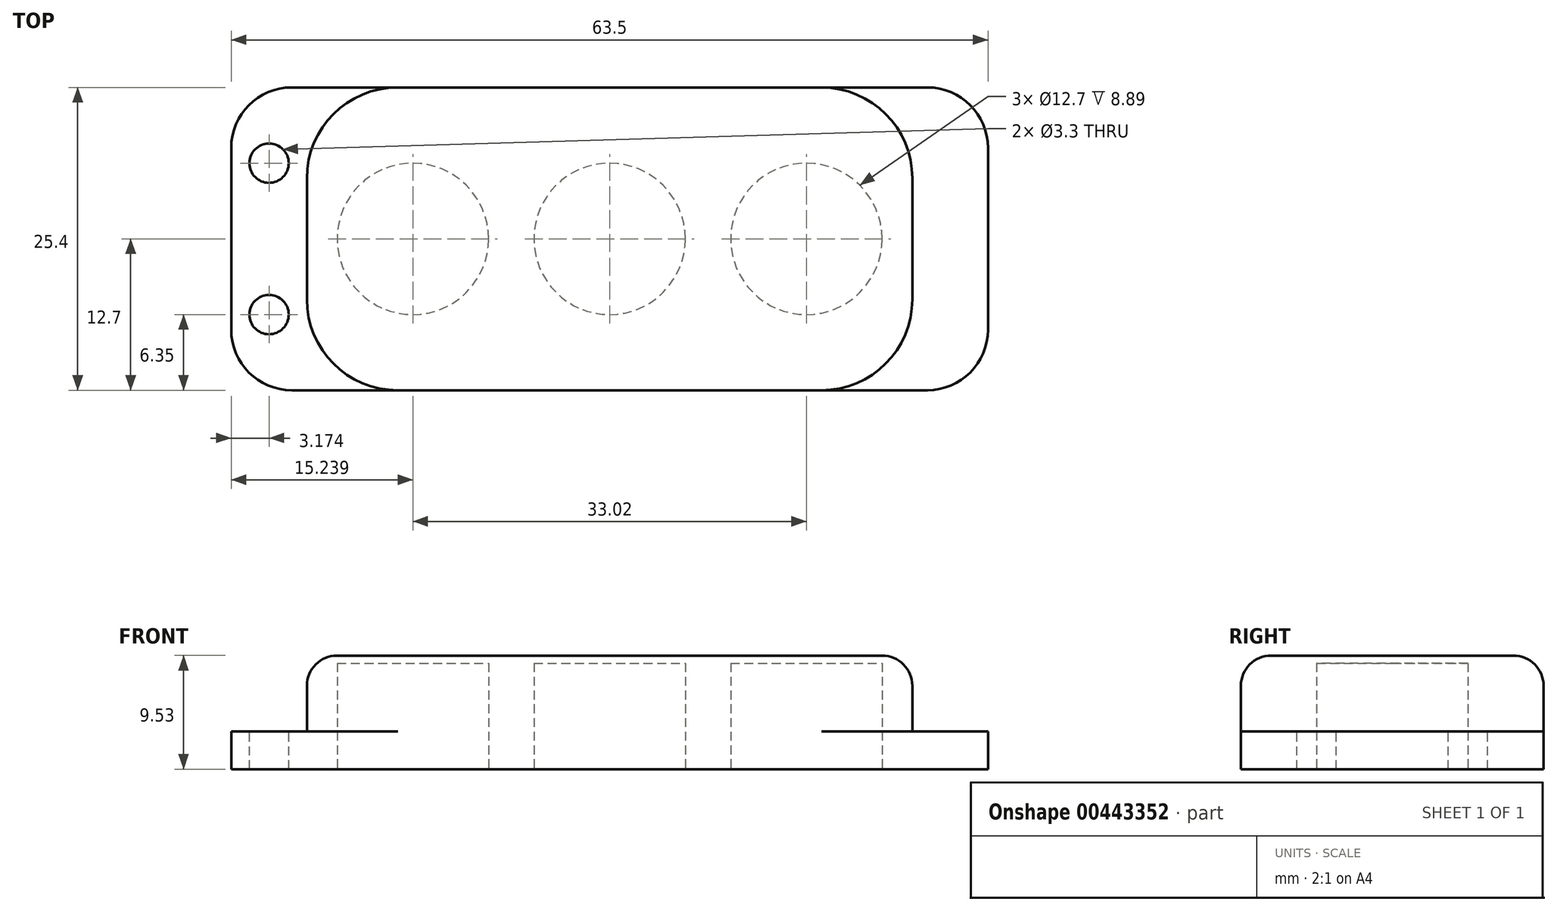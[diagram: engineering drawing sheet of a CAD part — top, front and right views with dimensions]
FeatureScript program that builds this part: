
annotation { "Feature Type Name" : "Feature", "Feature Type Description" : "" }
export const myFeature = defineFeature(function(context is Context, id is Id, definition is map)
    precondition{}
    {
        {
            var Q0;
            Q0=qCreatedBy(makeId("Front.planeOp"),FACE);
            var sketch = newSketch(context, id + "F0", { "sketchPlane" : qUnion([Q0])});
            skLineSegment(sketch, "E0.bottom", {"start": v(-44, 0) * mm, "end": v(19.5, 0) * mm});
            skLineSegment(sketch, "E0.top", {"start": v(-37.64, 9.52) * mm, "end": v(13.16, 9.52) * mm});
            skLineSegment(sketch, "E0.left", {"start": v(-44, 0) * mm, "end": v(-44, 3.18) * mm});
            skLineSegment(sketch, "E0.right", {"start": v(19.5, 0) * mm, "end": v(19.5, 3.17) * mm});
            skLineSegment(sketch, "E1.top", {"start": v(-44, 3.17) * mm, "end": v(-37.64, 3.17) * mm});
            skLineSegment(sketch, "E1.right", {"start": v(-37.64, 9.52) * mm, "end": v(-37.64, 3.17) * mm});
            skLineSegment(sketch, "E2.top", {"start": v(19.5, 3.17) * mm, "end": v(13.16, 3.17) * mm});
            skLineSegment(sketch, "E2.right", {"start": v(13.16, 9.52) * mm, "end": v(13.16, 3.17) * mm});
            skLineSegment(sketch, "E3", {"start": v(-12.24, 9.52) * mm, "end": v(-12.24, 0) * mm, "construction": true});
            skSolve(sketch);
        }
        {
            var Q0;
            Q0 = qSketchRegion(id + "F0", true);
            extrude(context, id + "F1", {"entities" : qUnion([Q0]), "depth" : 25.4 * mm});
        }
        {
            var Q0;
            Q0=makeQuery(id+"F1.opExtrude","SWEPT_FACE",FACE,{"disambiguationData":[OSD([sQuery(id+"F0.wireOp",EDGE,"E0.top")])]});
            var sketch = newSketch(context, id + "F2", { "sketchPlane" : qUnion([Q0])});
            skPoint(sketch, "E4", {"position": v(4.27, -12.7) * mm});
            skPoint(sketch, "E5", {"position": v(-28.75, -12.7) * mm});
            skCircle(sketch, "E6", {"center": v(-28.75, -12.7) * mm, "radius": 6.48 * mm});
            skCircle(sketch, "E7", {"center": v(4.27, -12.7) * mm, "radius": 6.48 * mm});
            skSolve(sketch);
        }
        {
            var Q0;
            Q0=makeQuery(id+"F1.opExtrude","SWEPT_FACE",FACE,{"disambiguationData":[OSD([sQuery(id+"F0.wireOp",EDGE,"E1.top")])]});
            var sketch = newSketch(context, id + "F3", { "sketchPlane" : qUnion([Q0])});
            skPoint(sketch, "E8", {"position": v(-40.82, -19.05) * mm});
            skPoint(sketch, "E9", {"position": v(-40.82, -6.35) * mm});
            skCircle(sketch, "E10", {"center": v(-40.82, -19.05) * mm, "radius": 1.65 * mm});
            skCircle(sketch, "E11", {"center": v(-40.82, -6.35) * mm, "radius": 1.65 * mm});
            skPoint(sketch, "E12.0", {"position": v(-12.24, -25.4) * mm});
            skLineSegment(sketch, "E13", {"start": v(-12.24, -25.4) * mm, "end": v(-12.24, 0) * mm});
            skCircle(sketch, "E14.MirrorC", {"center": v(16.33, -6.35) * mm, "radius": 1.65 * mm});
            skCircle(sketch, "E15.MirrorC", {"center": v(16.33, -19.05) * mm, "radius": 1.65 * mm});
            skSolve(sketch);
        }
        {
            var Q0;
            Q0=makeQuery(id+"F3.imprint","IMPRINT",FACE,{"disambiguationData":[TD([[makeQuery(id+"F3.imprint","IMPRINT",EDGE,{"derivedFrom":sQuery(id+"F3.wireOp",EDGE,"E10")}),1.0]])]});
            var Q1;
            Q1=makeQuery(id+"F3.imprint","IMPRINT",FACE,{"disambiguationData":[TD([[makeQuery(id+"F3.imprint","IMPRINT",EDGE,{"derivedFrom":sQuery(id+"F3.wireOp",EDGE,"E11")}),1.0]])]});
            var Q2;
            Q2=makeQuery(id+"F3.imprint","IMPRINT",FACE,{"disambiguationData":[TD([[makeQuery(id+"F3.imprint","IMPRINT",EDGE,{"derivedFrom":sQuery(id+"F3.wireOp",EDGE,"fb4f4f7a-e8af-40d2-be97-37f52cc8ef450.MirrorC")}),-1.0]])]});
            var Q3;
            Q3=makeQuery(id+"F3.imprint","IMPRINT",FACE,{"disambiguationData":[TD([[makeQuery(id+"F3.imprint","IMPRINT",EDGE,{"derivedFrom":sQuery(id+"F3.wireOp",EDGE,"d004ccc5-d1c6-44e7-8c95-f3ccb0f429bf0.MirrorC")}),-1.0]])]});
            var Q4;
            Q4=makeQuery(id+"F3.imprint","IMPRINT",FACE,{"disambiguationData":[TD([[makeQuery(id+"F3.imprint","IMPRINT",EDGE,{"derivedFrom":sQuery(id+"F3.wireOp",EDGE,"E14.MirrorC")}),-1.0]])]});
            var Q5;
            Q5=makeQuery(id+"F3.imprint","IMPRINT",FACE,{"disambiguationData":[TD([[makeQuery(id+"F3.imprint","IMPRINT",EDGE,{"derivedFrom":sQuery(id+"F3.wireOp",EDGE,"E15.MirrorC")}),-1.0]])]});
            extrude(context, id + "F4", {"entities" : qUnion([Q0, Q1, Q2, Q3, Q4, Q5]), "operationType" : NewBodyOperationType.REMOVE, "endBound" : BoundingType.THROUGH_ALL, "oppositeDirection" : true, "depth" : 25.4 * mm});
        }
        {
            var Q0;
            Q0=makeQuery(id+"F1.opExtrude","SWEPT_FACE",FACE,{"disambiguationData":[OSD([sQuery(id+"F0.wireOp",EDGE,"E0.bottom")])]});
            var sketch = newSketch(context, id + "F5", { "sketchPlane" : qUnion([Q0])});
            skPoint(sketch, "E16.0", {"position": v(-28.75, 12.7) * mm});
            skPoint(sketch, "E17.0", {"position": v(4.27, 12.7) * mm});
            skCircle(sketch, "E18", {"center": v(-28.75, 12.7) * mm, "radius": 6.35 * mm});
            skCircle(sketch, "E19", {"center": v(4.27, 12.7) * mm, "radius": 6.35 * mm});
            skCircle(sketch, "E20", {"center": v(-12.24, 12.7) * mm, "radius": 6.35 * mm});
            skPoint(sketch, "E20.centerSnap0", {"position": v(-12.24, 0) * mm});
            skSolve(sketch);
        }
        {
            var Q0;
            Q0 = qSketchRegion(id + "F5", true);
            extrude(context, id + "F6", {"entities" : qUnion([Q0]), "operationType" : NewBodyOperationType.REMOVE, "oppositeDirection" : true, "depth" : 8.9 * mm});
        }
        {
            var Q0;
            Q0=makeQuery(id+"F1.opExtrude","CAP_EDGE",EDGE,{"disambiguationData":[OSD([sQuery(id+"F0.wireOp",EDGE,"E0.right")])],"isStart":false});
            var Q1;
            Q1=makeQuery(id+"F1.opExtrude","CAP_EDGE",EDGE,{"disambiguationData":[OSD([sQuery(id+"F0.wireOp",EDGE,"E0.right")])],"isStart":true});
            var Q2;
            Q2=makeQuery(id+"F1.opExtrude","CAP_EDGE",EDGE,{"disambiguationData":[OSD([sQuery(id+"F0.wireOp",EDGE,"E0.left")])],"isStart":false});
            var Q3;
            Q3=makeQuery(id+"F1.opExtrude","CAP_EDGE",EDGE,{"disambiguationData":[OSD([sQuery(id+"F0.wireOp",EDGE,"E0.left")])],"isStart":true});
            fillet(context, id + "F7", {"entities" : qUnion([Q0, Q1, Q2, Q3]), "radius" : 5.08 * mm, "tangentPropagation" : true, "allowEdgeOverflow" : false});
        }
        {
            var Q0;
            Q0=makeQuery(id+"F1.opExtrude","CAP_EDGE",EDGE,{"disambiguationData":[OSD([sQuery(id+"F0.wireOp",EDGE,"E0.top")])],"isStart":false});
            var Q1;
            Q1=makeQuery(id+"F1.opExtrude","SWEPT_EDGE",EDGE,{"disambiguationData":[OSD([sQuery(id+"F0.wireOp",EDGE,"E0.top"),sQuery(id+"F0.wireOp",EDGE,"E1.right")])]});
            var Q2;
            Q2=makeQuery(id+"F1.opExtrude","CAP_EDGE",EDGE,{"disambiguationData":[OSD([sQuery(id+"F0.wireOp",EDGE,"E0.top")])],"isStart":true});
            var Q3;
            Q3=makeQuery(id+"F1.opExtrude","SWEPT_EDGE",EDGE,{"disambiguationData":[OSD([sQuery(id+"F0.wireOp",EDGE,"E0.top"),sQuery(id+"F0.wireOp",EDGE,"E2.right")])]});
            fillet(context, id + "F8", {"entities" : qUnion([Q0, Q1, Q2, Q3]), "radius" : 2.54 * mm, "tangentPropagation" : true, "allowEdgeOverflow" : false});
        }
        {
            var Q0;
            Q0=makeQuery(id+"F1.opExtrude","CAP_EDGE",EDGE,{"disambiguationData":[OSD([sQuery(id+"F0.wireOp",EDGE,"E1.right")])],"isStart":false});
            var Q1;
            Q1=makeQuery(id+"F1.opExtrude","CAP_EDGE",EDGE,{"disambiguationData":[OSD([sQuery(id+"F0.wireOp",EDGE,"E2.right")])],"isStart":false});
            var Q2;
            Q2=makeQuery(id+"F1.opExtrude","CAP_EDGE",EDGE,{"disambiguationData":[OSD([sQuery(id+"F0.wireOp",EDGE,"E1.right")])],"isStart":true});
            var Q3;
            Q3=makeQuery(id+"F1.opExtrude","CAP_EDGE",EDGE,{"disambiguationData":[OSD([sQuery(id+"F0.wireOp",EDGE,"E2.right")])],"isStart":true});
            fillet(context, id + "F9", {"entities" : qUnion([Q0, Q1, Q2, Q3]), "radius" : 7.62 * mm, "tangentPropagation" : true, "allowEdgeOverflow" : false});
        }
    });
